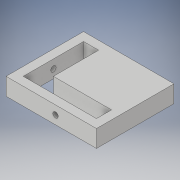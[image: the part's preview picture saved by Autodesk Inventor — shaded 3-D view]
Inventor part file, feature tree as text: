
AUTODESK INVENTOR PART (.ipt)
format: ipt  version: 2019 (Build 230136000, 136)  size: 125,952 bytes
history: native  units: in
note: dims shown in document units (in); Inventor stores cm internally (conversion verified against a paired STEP export)
features: sketch x3, hole x2, extrude x1
ambient origin geometry x8: Origin, YZ Plane, XZ Plane, XY Plane, X Axis, Y Axis, Z Axis, Center Point
bodies: Solid1 (feature_tree)
feature tree (6):
  extrude  "Extrusion1"  Depth=5.25in
  hole  "Hole1"  [1 undecoded]
  hole  "Hole2"  [1 undecoded]
  sketch  "Sketch1"  dims[d0=4.5in d1=5.25in]
  sketch  "Sketch3"  dims[d2=0.5in d3=0.5in]
  sketch  "Sketch4"  dims[d4=0.5in d5=0.5in d6=0.875in d7=0.875in d8=1.0in d9=0.0in d10=4.75in d11=1.0in d12=2.375in d13=0.5in d14=0.3091in d15=0.276in d16=0.375in d17=0.25in d18=0.5635in d19=1.0in d20=0.8108in d21=1.0in d22=4.5in d23=0.5in d24=2.25in d25=0.3091in d26=0.276in d27=0.375in d28=0.25in d29=0.5635in d30=1.0in d31=0.0in]
note: 2 required parameter values undecoded (feature->parameter linkage not recoverable at this tier; creation-order binding heuristic only, values carry confidence <= 0.55)
